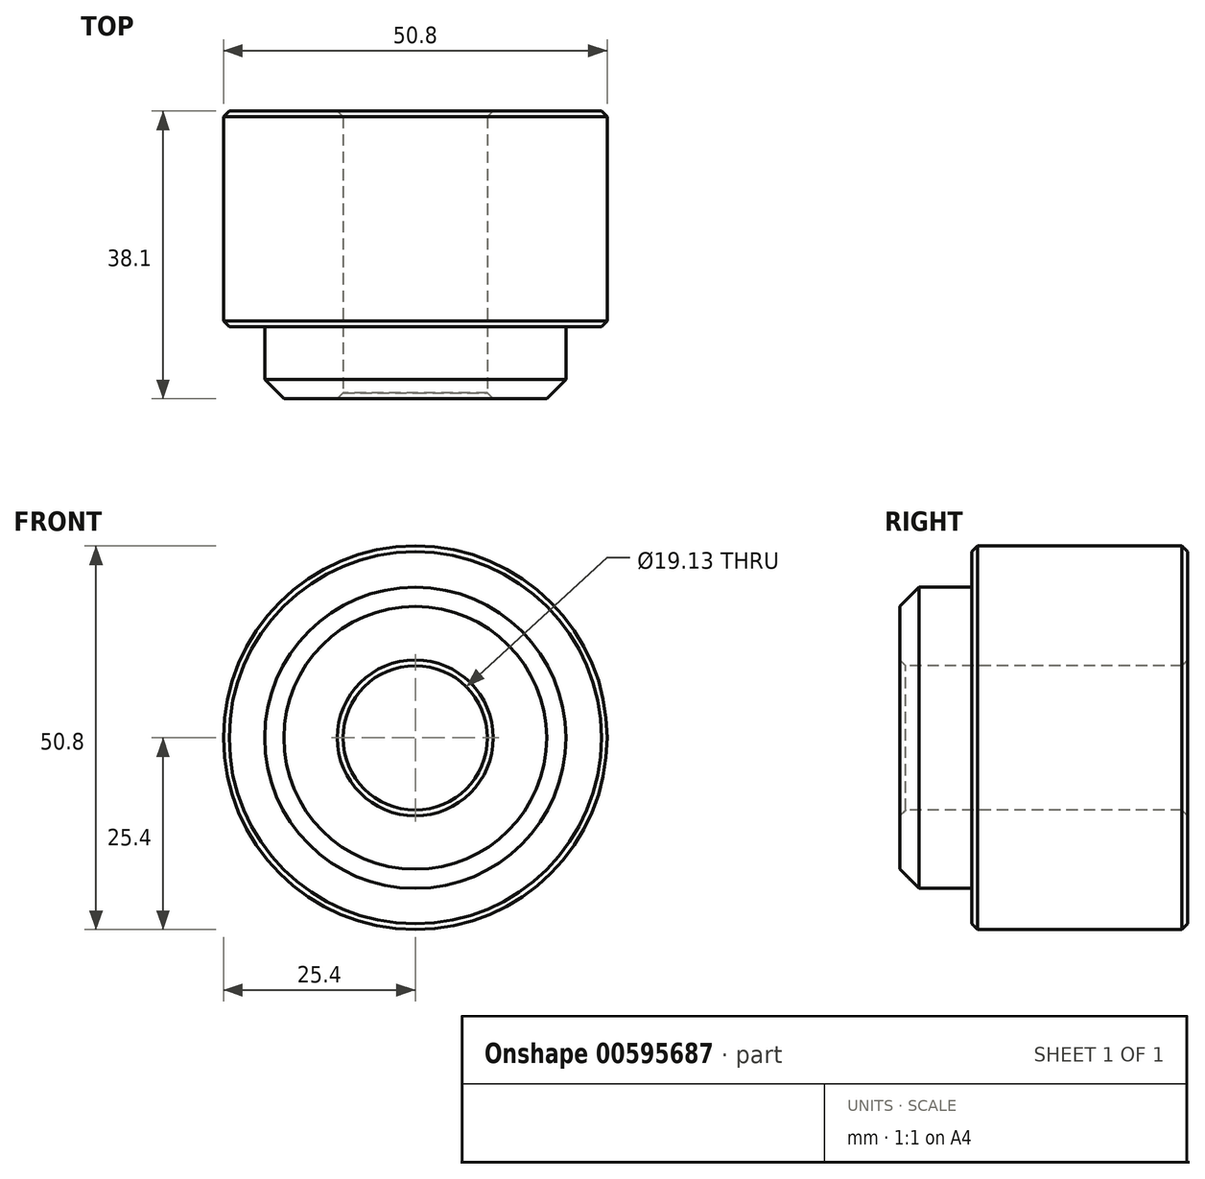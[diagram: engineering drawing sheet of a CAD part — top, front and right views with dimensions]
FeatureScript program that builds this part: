
annotation { "Feature Type Name" : "Feature", "Feature Type Description" : "" }
export const myFeature = defineFeature(function(context is Context, id is Id, definition is map)
    precondition{}
    {
        {
            var Q0;
            Q0=qCreatedBy(makeId("Right.planeOp"),FACE);
            var sketch = newSketch(context, id + "F0", { "sketchPlane" : qUnion([Q0])});
            skLineSegment(sketch, "E0", {"start": v(0, 19.94) * mm, "end": v(9.53, 19.94) * mm});
            skLineSegment(sketch, "E1", {"start": v(9.52, 19.94) * mm, "end": v(9.52, 25.4) * mm});
            skLineSegment(sketch, "E2", {"start": v(9.52, 25.4) * mm, "end": v(38.1, 25.4) * mm});
            skLineSegment(sketch, "E3", {"start": v(38.1, 25.4) * mm, "end": v(38.1, 9.56) * mm});
            skLineSegment(sketch, "E4", {"start": v(38.1, 9.56) * mm, "end": v(0, 9.56) * mm});
            skLineSegment(sketch, "E5", {"start": v(0, 9.56) * mm, "end": v(0, 19.94) * mm});
            skLineSegment(sketch, "E6", {"start": v(0, 0) * mm, "end": v(17.26, 0) * mm, "construction": true});
            skSolve(sketch);
        }
        {
            var Q0;
            Q0 = qSketchRegion(id + "F0", true);
            var Q1;
            Q1=sQuery(id+"F0.wireOp",EDGE,"E6");
            revolve(context, id + "F1", {"entities" : qUnion([Q0]), "axis" : qUnion([Q1]), "revolveType" : RevolveType.FULL});
        }
        {
            var Q0;
            Q0=makeQuery(id+"F1.opRevolve","SWEPT_EDGE",EDGE,{"disambiguationData":[OSD([sQuery(id+"F0.wireOp",EDGE,"E0"),sQuery(id+"F0.wireOp",EDGE,"E5")])]});
            chamfer(context, id + "F2", {"entities" : qUnion([Q0]), "width" : 2.54 * mm, "tangentPropagation" : true});
        }
        {
            var Q0;
            Q0=makeQuery(id+"F1.opRevolve","SWEPT_FACE",FACE,{"disambiguationData":[OSD([sQuery(id+"F0.wireOp",EDGE,"E4")])]});
            var Q1;
            Q1=makeQuery(id+"F1.opRevolve","SWEPT_FACE",FACE,{"disambiguationData":[OSD([sQuery(id+"F0.wireOp",EDGE,"E2")])]});
            chamfer(context, id + "F3", {"entities" : qUnion([Q0, Q1]), "width" : 0.76 * mm, "tangentPropagation" : true});
        }
    });
